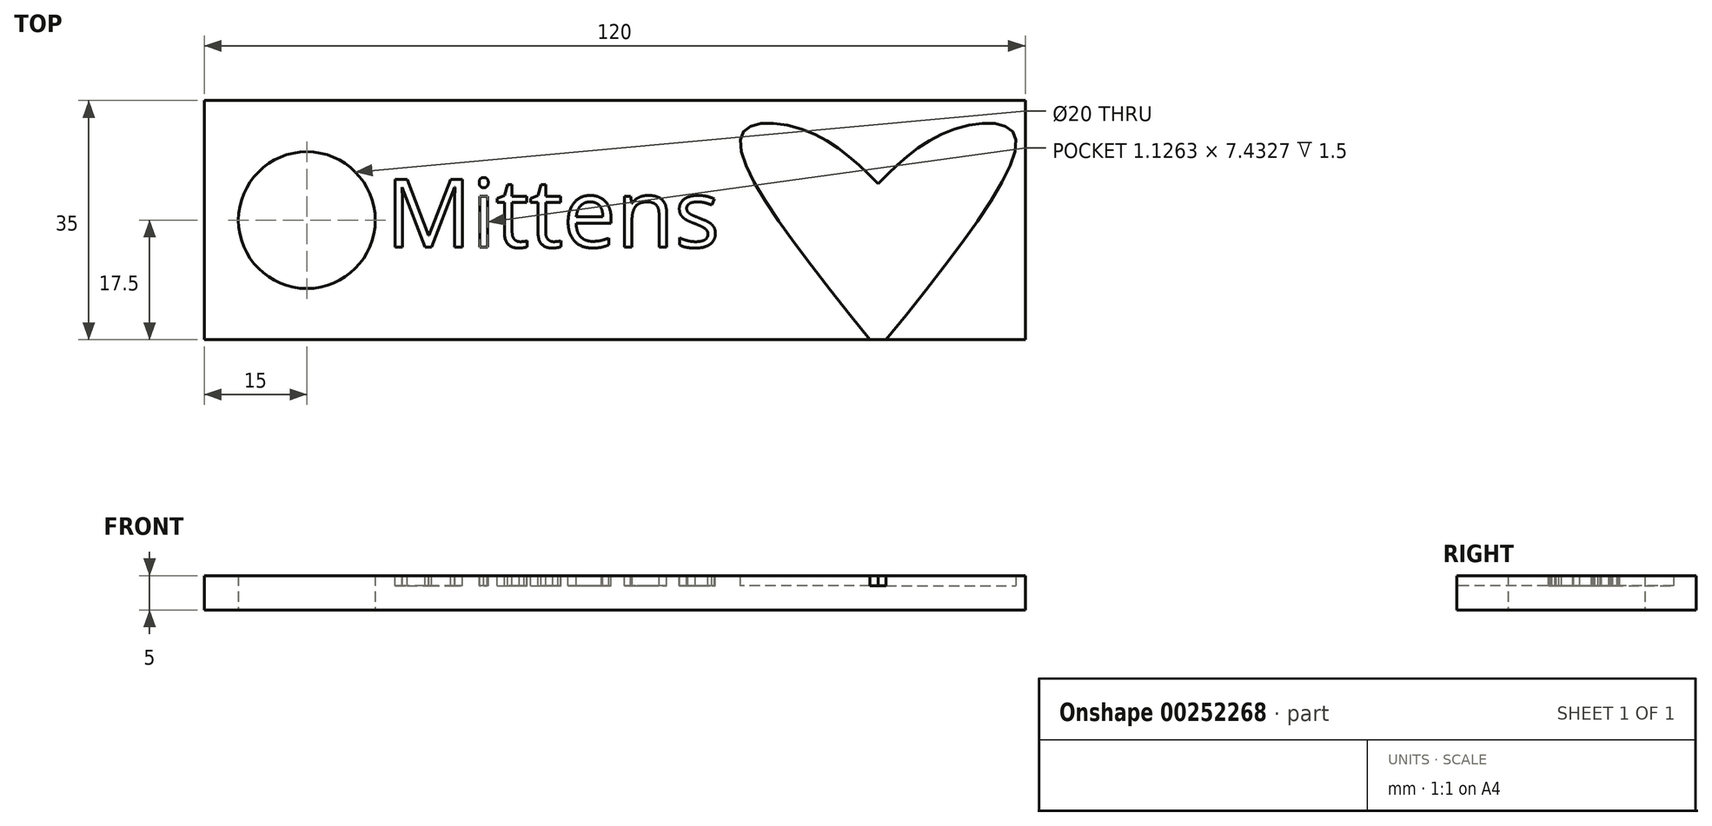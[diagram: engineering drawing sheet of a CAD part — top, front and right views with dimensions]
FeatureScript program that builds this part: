
annotation { "Feature Type Name" : "Feature", "Feature Type Description" : "" }
export const myFeature = defineFeature(function(context is Context, id is Id, definition is map)
    precondition{}
    {
        {
            var Q0;
            Q0=qCreatedBy(makeId("Top.planeOp"),FACE);
            var sketch = newSketch(context, id + "F0", { "sketchPlane" : qUnion([Q0])});
            skLineSegment(sketch, "E0.bottom", {"start": v(60, -17.5) * mm, "end": v(-60, -17.5) * mm});
            skLineSegment(sketch, "E0.top", {"start": v(60, 17.5) * mm, "end": v(-60, 17.5) * mm});
            skLineSegment(sketch, "E0.left", {"start": v(60, -17.5) * mm, "end": v(60, 17.5) * mm});
            skLineSegment(sketch, "E0.right", {"start": v(-60, -17.5) * mm, "end": v(-60, 17.5) * mm});
            skPoint(sketch, "E0.middle", {"position": v(0, 0) * mm});
            skCircle(sketch, "E1", {"center": v(-45, 0) * mm, "radius": 10 * mm});
            skSolve(sketch);
        }
        {
            var Q0;
            Q0=makeQuery(id+"F0.imprint","IMPRINT",FACE,{"disambiguationData":[TD([[makeQuery(id+"F0.imprint","IMPRINT",EDGE,{"derivedFrom":sQuery(id+"F0.wireOp",EDGE,"E0.bottom")}),-1.0]])]});
            extrude(context, id + "F1", {"entities" : qUnion([Q0]), "depth" : 5 * mm});
        }
        {
            var Q0;
            Q0=makeQuery(id+"F1.opExtrude","CAP_FACE",FACE,{"disambiguationData":[OSD([sQuery(id+"F0.wireOp",EDGE,"E0.bottom"),sQuery(id+"F0.wireOp",EDGE,"E0.top"),sQuery(id+"F0.wireOp",EDGE,"E0.left"),sQuery(id+"F0.wireOp",EDGE,"E0.right"),sQuery(id+"F0.wireOp",EDGE,"E1")])],"isStart":false});
            var sketch = newSketch(context, id + "F2", { "sketchPlane" : qUnion([Q0])});
            skText(sketch, "E2", { "text": "Mittens\n", "fontName": "OpenSans-Regular.ttf"});
            const initialGuessF2  = {"E2": [-0.03345, -0.00395, 1, 0, 0.01]};
            skSetInitialGuess(sketch, initialGuessF2);
            skSolve(sketch);
        }
        {
            var Q0;
            Q0=makeQuery(id+"F2.imprint","IMPRINT",FACE,{"disambiguationData":[TD([[makeQuery(id+"F2.imprint","IMPRINT",EDGE,{"derivedFrom":sQuery(id+"F2.wireOp",EDGE,"E2.sketch_text.stroke-0")}),1.0]])]});
            var sketch = newSketch(context, id + "F3", { "sketchPlane" : qUnion([Q0])});
            skLineSegment(sketch, "E3", {"start": v(38.49, 17.47) * mm, "end": v(38.49, -18.95) * mm, "construction": true});
            skFitSpline(sketch, "E4", {"points": [v(38.49, 5.33) * mm, v(28.12, 13.03) * mm, v(18.65, 12.73) * mm, v(38.49, -18.95) * mm], "startDerivative": vector(-32.4, 32.36) * mm, "endDerivative": vector(69.64, -86.45) * mm});
            skFitSpline(sketch, "E5.MirrorCS", {"points": [v(38.49, 5.33) * mm, v(48.85, 13.03) * mm, v(58.32, 12.73) * mm, v(38.49, -18.95) * mm], "startDerivative": vector(32.4, 32.36) * mm, "endDerivative": vector(-69.64, -86.45) * mm});
            skFitSpline(sketch, "E6.MirrorCS", {"points": [v(38.49, 5.33) * mm, v(48.85, 13.03) * mm, v(58.32, 12.73) * mm, v(38.49, -18.95) * mm], "startDerivative": vector(32.4, 32.36) * mm, "endDerivative": vector(-69.64, -86.45) * mm});
            skSolve(sketch);
        }
        {
            var Q0;
            Q0 = qSketchRegion(id + "F2", true);
            extrude(context, id + "F4", {"entities" : qUnion([Q0]), "operationType" : NewBodyOperationType.REMOVE, "depth" : 1.5 * mm});
        }
        {
            var Q0;
            Q0 = qSketchRegion(id + "F3", true);
            extrude(context, id + "F5", {"entities" : qUnion([Q0]), "operationType" : NewBodyOperationType.REMOVE, "oppositeDirection" : true, "depth" : 1.5 * mm});
        }
        {
            var Q0;
            Q0 = qSketchRegion(id + "F2", true);
            extrude(context, id + "F6", {"entities" : qUnion([Q0]), "operationType" : NewBodyOperationType.REMOVE, "oppositeDirection" : true, "depth" : 1.5 * mm});
        }
    });
